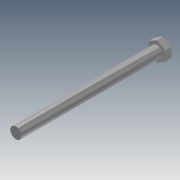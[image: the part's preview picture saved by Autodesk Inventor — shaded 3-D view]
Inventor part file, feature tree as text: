
AUTODESK INVENTOR PART (.ipt)
format: ipt  version: 2014 (Build 180170000, 170)  size: 95,232 bytes
history: native  units: in
note: dims shown in document units (in); Inventor stores cm internally (conversion verified against a paired STEP export)
features: extrude x3, sketch x3
ambient origin geometry x8: Origin, YZ Plane, XZ Plane, XY Plane, X Axis, Y Axis, Z Axis, Center Point
bodies: Solid1 (feature_tree)
feature tree (6):
  extrude  "Extrusion1"  Depth=0.23in TaperAngle=0.0deg
  extrude  "Extrusion2"  Depth=5.0in TaperAngle=0.0deg
  extrude  "Extrusion3"  [1 undecoded]
  sketch  "Sketch1"  dims[d0=0.5625in d1=0.23in d2=0.0in]
  sketch  "Sketch2"  dims[d3=0.375in d4=5.0in d5=0.0in]
  sketch  "Sketch3"  dims[d6=5.0in d7=60.0deg]
note: 1 required parameter value undecoded (feature->parameter linkage not recoverable at this tier; creation-order binding heuristic only, values carry confidence <= 0.55)
